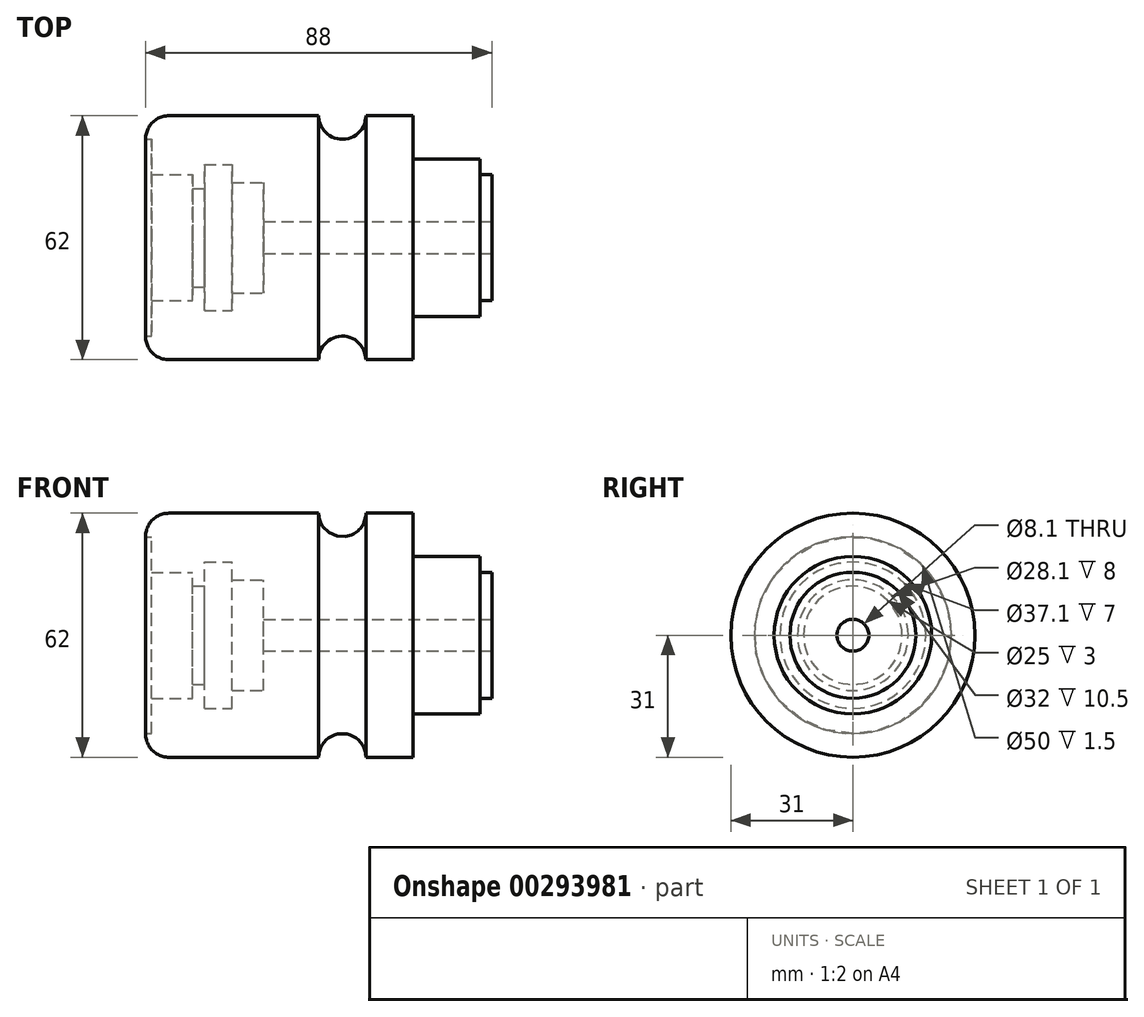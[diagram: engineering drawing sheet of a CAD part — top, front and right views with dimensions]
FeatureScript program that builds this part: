
annotation { "Feature Type Name" : "Feature", "Feature Type Description" : "" }
export const myFeature = defineFeature(function(context is Context, id is Id, definition is map)
    precondition{}
    {
        {
            var Q0;
            Q0=qCreatedBy(makeId("Top.planeOp"),FACE);
            var sketch = newSketch(context, id + "F0", { "sketchPlane" : qUnion([Q0])});
            skLineSegment(sketch, "E0", {"start": v(0, 0) * mm, "end": v(0, 31) * mm});
            skLineSegment(sketch, "E1", {"start": v(0, 31) * mm, "end": v(68, 31) * mm});
            skLineSegment(sketch, "E2", {"start": v(68, 31) * mm, "end": v(68, 20) * mm});
            skLineSegment(sketch, "E3", {"start": v(68, 20) * mm, "end": v(85, 20) * mm});
            skLineSegment(sketch, "E4", {"start": v(85, 20) * mm, "end": v(85, 16) * mm});
            skLineSegment(sketch, "E5", {"start": v(85, 16) * mm, "end": v(88, 16) * mm});
            skLineSegment(sketch, "E6", {"start": v(88, 16) * mm, "end": v(88, 0) * mm});
            skLineSegment(sketch, "E7", {"start": v(88, 0) * mm, "end": v(0, 0) * mm});
            skLineSegment(sketch, "E8", {"start": v(0, 0) * mm, "end": v(99.73, 0) * mm, "construction": true});
            skSolve(sketch);
        }
        {
            var Q0;
            Q0=makeQuery(id+"F0.imprint","IMPRINT",FACE,{"disambiguationData":[TD([[makeQuery(id+"F0.imprint","IMPRINT",EDGE,{"derivedFrom":sQuery(id+"F0.wireOp",EDGE,"E0")}),-1.0]])]});
            var Q1;
            Q1=sQuery(id+"F0.wireOp",EDGE,"E8");
            revolve(context, id + "F1", {"entities" : qUnion([Q0]), "axis" : qUnion([Q1]), "revolveType" : RevolveType.FULL});
        }
        {
            var Q0;
            Q0=makeQuery(id+"F1.opRevolve","SWEPT_EDGE",EDGE,{"disambiguationData":[OSD([sQuery(id+"F0.wireOp",EDGE,"E0"),sQuery(id+"F0.wireOp",EDGE,"E1")])]});
            fillet(context, id + "F2", {"entities" : qUnion([Q0]), "radius" : 6 * mm, "tangentPropagation" : true, "allowEdgeOverflow" : false});
        }
        {
            var Q0;
            Q0=qCreatedBy(makeId("Top.planeOp"),FACE);
            var sketch = newSketch(context, id + "F3", { "sketchPlane" : qUnion([Q0])});
            skCircle(sketch, "E9", {"center": v(50, 31) * mm, "radius": 6 * mm});
            skSolve(sketch);
        }
        {
            var Q0;
            Q0=makeQuery(id+"F3.imprint","IMPRINT",FACE,{"disambiguationData":[TD([[makeQuery(id+"F3.imprint","IMPRINT",EDGE,{"derivedFrom":sQuery(id+"F3.wireOp",EDGE,"E9")}),1.0]])]});
            var Q1;
            Q1=sQuery(id+"F0.wireOp",EDGE,"E8");
            revolve(context, id + "F4", {"operationType" : NewBodyOperationType.REMOVE, "entities" : qUnion([Q0]), "axis" : qUnion([Q1]), "revolveType" : RevolveType.FULL, "oppositeDirection" : true});
        }
        {
            var Q0;
            Q0=qCreatedBy(makeId("Top.planeOp"),FACE);
            var sketch = newSketch(context, id + "F5", { "sketchPlane" : qUnion([Q0])});
            skLineSegment(sketch, "E10", {"start": v(0, 0) * mm, "end": v(0, 25) * mm});
            skLineSegment(sketch, "E11", {"start": v(0, 25) * mm, "end": v(1.5, 25) * mm});
            skLineSegment(sketch, "E12", {"start": v(1.5, 25) * mm, "end": v(1.5, 16) * mm});
            skLineSegment(sketch, "E13", {"start": v(1.5, 16) * mm, "end": v(12, 16) * mm});
            skLineSegment(sketch, "E14", {"start": v(12, 16) * mm, "end": v(12, 12.5) * mm});
            skLineSegment(sketch, "E15", {"start": v(12, 12.5) * mm, "end": v(15, 12.5) * mm});
            skLineSegment(sketch, "E16", {"start": v(15, 12.5) * mm, "end": v(15, 18.55) * mm});
            skLineSegment(sketch, "E17", {"start": v(15, 18.55) * mm, "end": v(22, 18.55) * mm});
            skLineSegment(sketch, "E18", {"start": v(22, 18.55) * mm, "end": v(22, 14.05) * mm});
            skLineSegment(sketch, "E19", {"start": v(22, 14.05) * mm, "end": v(30, 14.05) * mm});
            skLineSegment(sketch, "E20", {"start": v(30, 14.05) * mm, "end": v(30, 4.05) * mm});
            skLineSegment(sketch, "E21", {"start": v(30, 4.05) * mm, "end": v(88, 4.05) * mm});
            skLineSegment(sketch, "E22", {"start": v(88, 4.05) * mm, "end": v(88, 0) * mm});
            skLineSegment(sketch, "E23", {"start": v(88, 0) * mm, "end": v(0, 0) * mm});
            skSolve(sketch);
        }
        {
            var Q0;
            Q0 = qSketchRegion(id + "F5", true);
            var Q1;
            Q1=sQuery(id+"F0.wireOp",EDGE,"E8");
            revolve(context, id + "F6", {"operationType" : NewBodyOperationType.REMOVE, "entities" : qUnion([Q0]), "axis" : qUnion([Q1]), "revolveType" : RevolveType.FULL, "oppositeDirection" : true});
        }
    });
